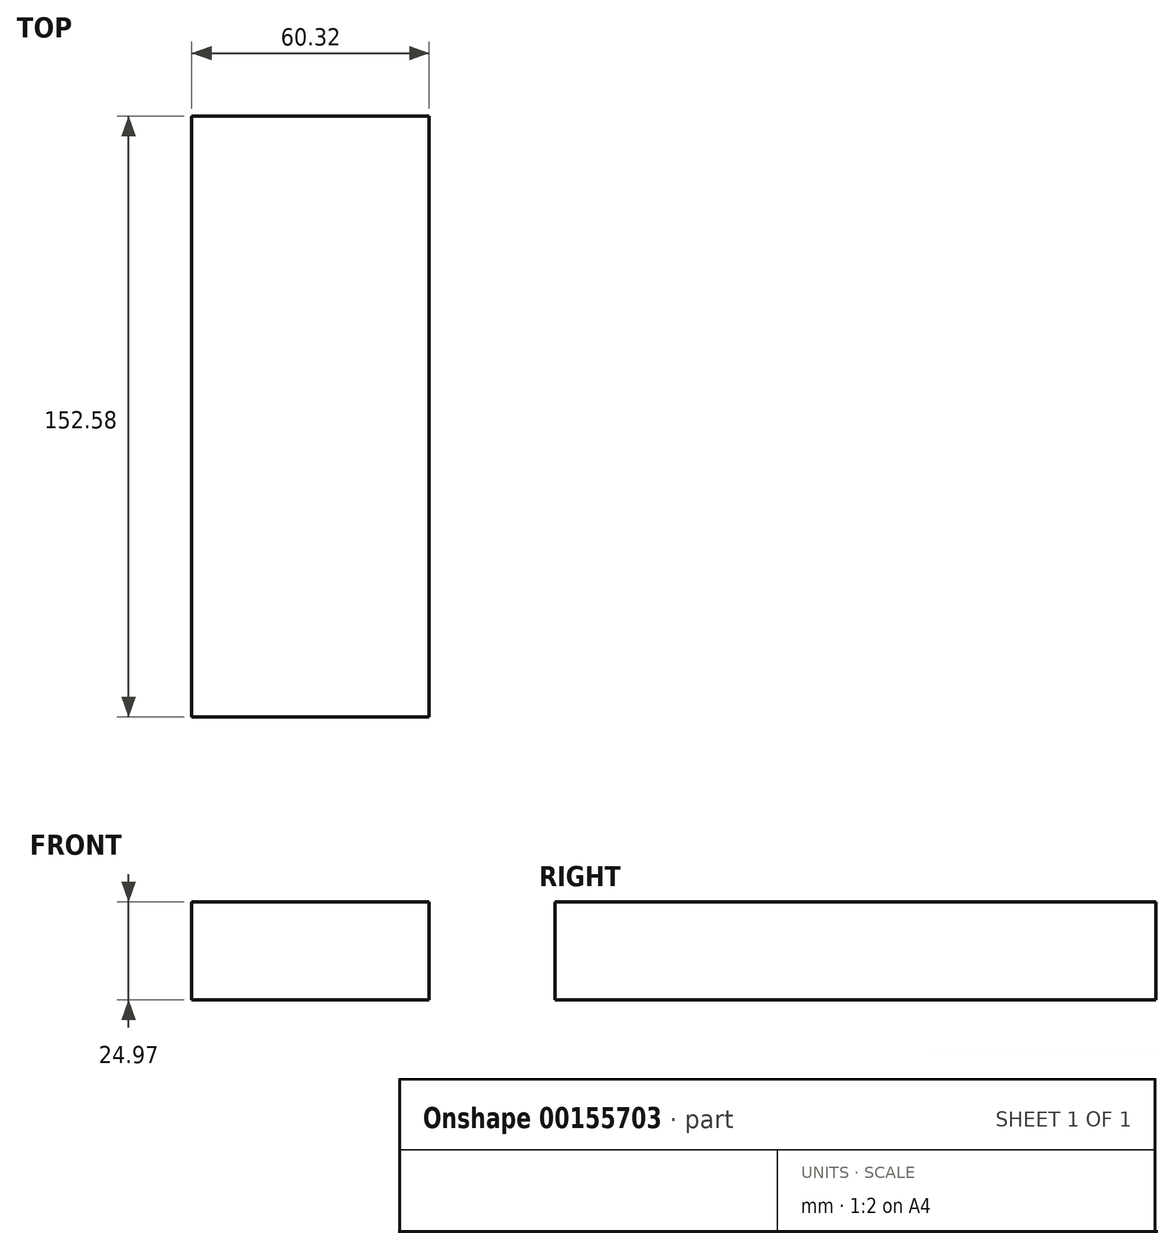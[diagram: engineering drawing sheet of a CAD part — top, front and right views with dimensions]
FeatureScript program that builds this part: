
annotation { "Feature Type Name" : "Feature", "Feature Type Description" : "" }
export const myFeature = defineFeature(function(context is Context, id is Id, definition is map)
    precondition{}
    {
        {
            var Q0;
            Q0=qCreatedBy(makeId("Right.planeOp"),FACE);
            var sketch = newSketch(context, id + "F0", { "sketchPlane" : qUnion([Q0])});
            skLineSegment(sketch, "E0.bottom", {"start": v(0, 0) * mm, "end": v(152.58, 0) * mm});
            skLineSegment(sketch, "E0.top", {"start": v(0, -24.97) * mm, "end": v(152.58, -24.97) * mm});
            skLineSegment(sketch, "E0.left", {"start": v(0, 0) * mm, "end": v(0, -24.97) * mm});
            skLineSegment(sketch, "E0.right", {"start": v(152.58, 0) * mm, "end": v(152.58, -24.97) * mm});
            skSolve(sketch);
        }
        {
            var Q0;
            Q0 = qSketchRegion(id + "F0", true);
            extrude(context, id + "F1", {"entities" : qUnion([Q0]), "depth" : 60.32 * mm});
        }
    });
